# Revit family: Terminal de control remoto_Aguilera Electronica
name_source: partatom
category: Equipos eléctricos
revit_build: Autodesk Revit 2017 (Build: 20160225_1515(x64)
units: mm (PartAtom-declared; Revit-internal decimal feet)

## family parameters
Anfitrión = Cara
Compartido = No
Configuración de panel = Dos columnas, circuitos en vertical
Corte con vacíos al cargar = No
Cota de conector redondo = Diámetro de uso
Número OmniClass = 23.85.30.21.11.14
Punto de cálculo de habitación = No
Tipo de pieza = Cuadro de control
Título OmniClass = Alarm Panels

## types (1)
- Terminal de control remoto
    Alto = 410 mm  [stored 1.34514 ft]
    Ancho = 310 mm  [stored 1.01706 ft]
    Comentarios de tipo = Dispone de fuente de alimentación independiente y capacidad para 2 baterías de 7 Ah.
Medidas: 410 x 310 x 120 mm
    Descripción = Terminal de control remoto fabricado por AGUILERA ELECTRÓNICA desarrollado para el control y gestión remota de las instalaciones de protección contra incendios basadas en nuestras centrales algorítmicas.
Este terminal permite controlar “a distancia” vía cable (RS-485) cualquier instalación basada en las centrales AE/SA-C1, AE/SA-C2 y AE/SA-C8.
La conexión se realiza en red, a través de un canal de comunicaciones RS-485.
Todos los paneles de control muestran el estado general de todas las centrales existentes en la red y desde cualquiera de ellos se puede controlar cualquier central.
    Diámetro tubo = 20 mm  [stored 0.0656168 ft]
    Elevación por defecto = 1200 mm
    Fabricante = Aguilera Electrónica
    Fondo = 120 mm  [stored 0.393701 ft]
    Modelo = AE/SA-TCR
    Potencia aparente = 460 VA
    Potencial eléctrico = 230 V
    Símbolo = Sí
    Símbolo texto modelo = Sí
    URL = http://aguilera.es

note: [stored X ft] marks values corroborated as IEEE doubles in the binary element streams (Revit-internal decimal feet)
